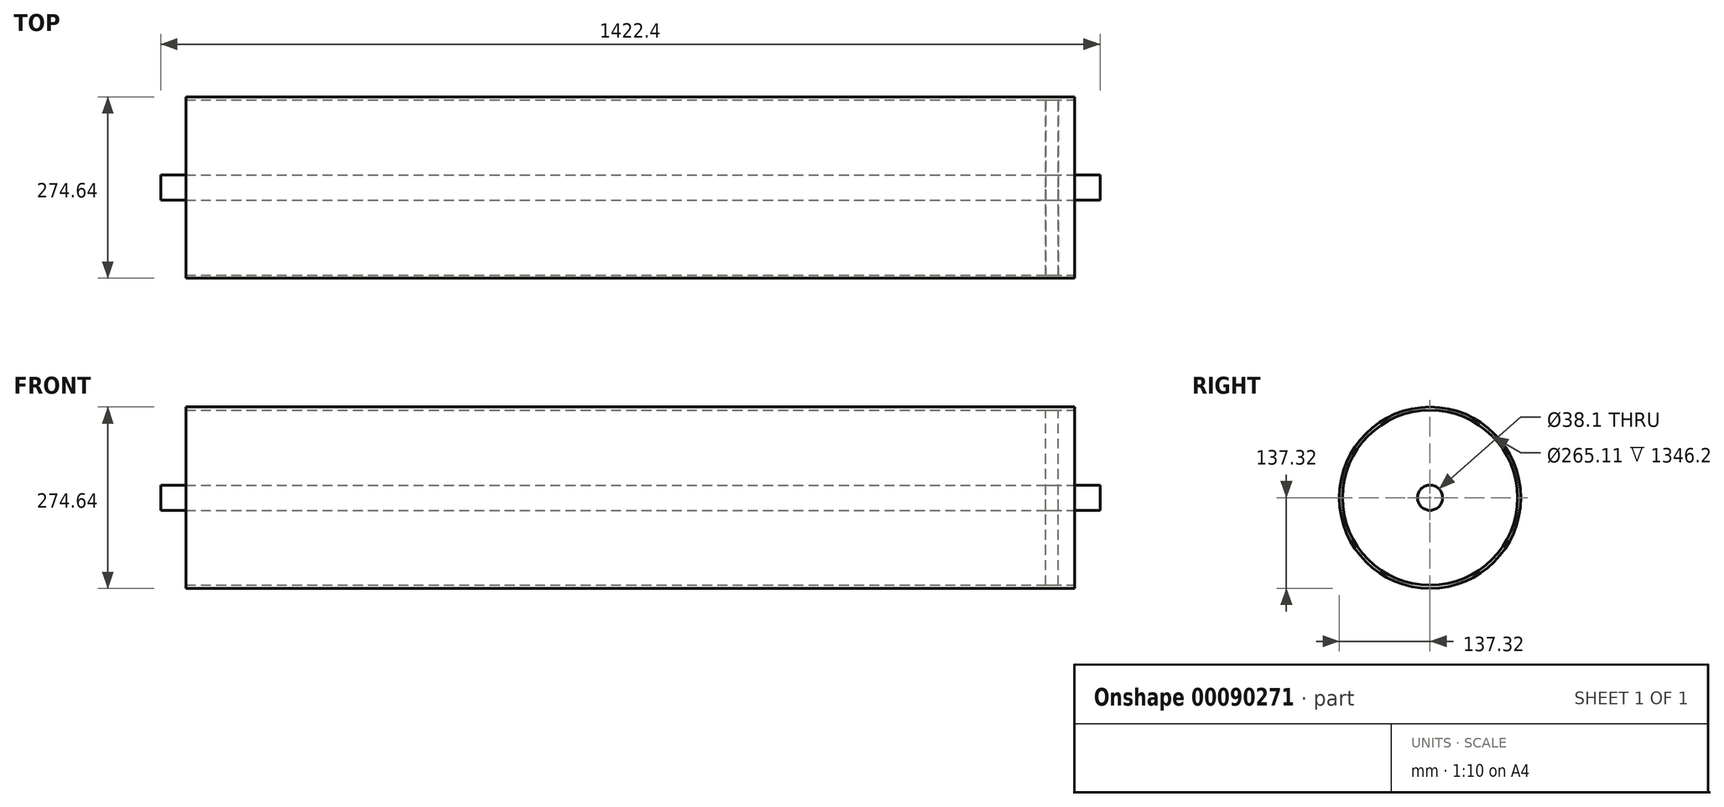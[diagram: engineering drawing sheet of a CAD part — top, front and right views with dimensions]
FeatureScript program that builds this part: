
annotation { "Feature Type Name" : "Feature", "Feature Type Description" : "" }
export const myFeature = defineFeature(function(context is Context, id is Id, definition is map)
    precondition{}
    {
        {
            var Q0;
            Q0=qCreatedBy(makeId("Top.planeOp"),FACE);
            var sketch = newSketch(context, id + "F0", { "sketchPlane" : qUnion([Q0])});
            skLineSegment(sketch, "E0.bottom", {"start": v(0, 0) * mm, "end": v(711.2, 0) * mm});
            skLineSegment(sketch, "E0.top", {"start": v(0, 19.05) * mm, "end": v(711.2, 19.05) * mm});
            skLineSegment(sketch, "E0.left", {"start": v(0, 0) * mm, "end": v(0, 19.05) * mm});
            skLineSegment(sketch, "E0.right", {"start": v(711.2, 0) * mm, "end": v(711.2, 19.05) * mm});
            skLineSegment(sketch, "E1.bottom", {"start": v(0, 137.32) * mm, "end": v(673.1, 137.32) * mm});
            skLineSegment(sketch, "E1.top", {"start": v(0, 132.56) * mm, "end": v(673.1, 132.56) * mm});
            skLineSegment(sketch, "E1.left", {"start": v(0, 137.32) * mm, "end": v(0, 132.56) * mm});
            skLineSegment(sketch, "E1.right", {"start": v(673.1, 137.32) * mm, "end": v(673.1, 132.56) * mm});
            skLineSegment(sketch, "E2", {"start": v(628.65, 19.05) * mm, "end": v(628.65, 132.56) * mm});
            skLineSegment(sketch, "E3", {"start": v(647.7, 132.56) * mm, "end": v(647.7, 19.05) * mm});
            skLineSegment(sketch, "E4.MirrorCS", {"start": v(-711.2, 0) * mm, "end": v(-711.2, 19.05) * mm});
            skLineSegment(sketch, "E5.MirrorCS", {"start": v(-673.1, 137.32) * mm, "end": v(-673.1, 132.56) * mm});
            skLineSegment(sketch, "E6.MirrorCS", {"start": v(0, 0) * mm, "end": v(-711.2, 0) * mm});
            skLineSegment(sketch, "E7.MirrorCS", {"start": v(-628.65, 19.05) * mm, "end": v(-628.65, 132.56) * mm});
            skLineSegment(sketch, "E8.MirrorCS", {"start": v(-647.7, 132.56) * mm, "end": v(-647.7, 19.05) * mm});
            skLineSegment(sketch, "E9.MirrorCS", {"start": v(0, 19.05) * mm, "end": v(-711.2, 19.05) * mm});
            skLineSegment(sketch, "E10.MirrorCS", {"start": v(0, 137.32) * mm, "end": v(-673.1, 137.32) * mm});
            skLineSegment(sketch, "E11.MirrorCS", {"start": v(0, 132.56) * mm, "end": v(-673.1, 132.56) * mm});
            skSolve(sketch);
        }
        {
            var Q0;
            {var subQ2=sQuery(id+"F0.wireOp",EDGE,"E0.left");Q0=makeQuery(id+"F0.imprint","IMPRINT",FACE,{"disambiguationData":[TD([[makeQuery(id+"F0.imprint","IMPRINT",EDGE,{"derivedFrom":subQ2}),1.0]])]});}
            var Q1;
            Q1=makeQuery(id+"F0.imprint","IMPRINT",FACE,{"disambiguationData":[TD([[makeQuery(id+"F0.imprint","IMPRINT",EDGE,{"derivedFrom":sQuery(id+"F0.wireOp",EDGE,"E0.bottom")}),1.0]])]});
            var Q2;
            Q2=sQuery(id+"F0.wireOp",EDGE,"E6.MirrorCS");
            revolve(context, id + "F1", {"entities" : qUnion([Q0, Q1]), "axis" : qUnion([Q2]), "revolveType" : RevolveType.FULL});
        }
        {
            var Q0;
            {var subQ0=sQuery(id+"F0.wireOp",EDGE,"E2");Q0=makeQuery(id+"F0.imprint","IMPRINT",FACE,{"disambiguationData":[TD([[makeQuery(id+"F0.imprint","IMPRINT",EDGE,{"derivedFrom":subQ0}),-1.0]])]});}
            var Q1;
            Q1=sQuery(id+"F0.wireOp",EDGE,"E6.MirrorCS");
            revolve(context, id + "F2", {"entities" : qUnion([Q0]), "axis" : qUnion([Q1]), "revolveType" : RevolveType.FULL});
        }
        {
            var Q0;
            {var subQ1=sQuery(id+"F0.wireOp",EDGE,"E1.left");Q0=makeQuery(id+"F0.imprint","IMPRINT",FACE,{"disambiguationData":[TD([[makeQuery(id+"F0.imprint","IMPRINT",EDGE,{"derivedFrom":subQ1}),-1.0]])]});}
            var Q1;
            Q1=makeQuery(id+"F0.imprint","IMPRINT",FACE,{"disambiguationData":[TD([[makeQuery(id+"F0.imprint","IMPRINT",EDGE,{"derivedFrom":sQuery(id+"F0.wireOp",EDGE,"E1.bottom")}),-1.0]])]});
            var Q2;
            Q2=sQuery(id+"F0.wireOp",EDGE,"E6.MirrorCS");
            revolve(context, id + "F3", {"entities" : qUnion([Q0, Q1]), "axis" : qUnion([Q2]), "revolveType" : RevolveType.FULL});
        }
    });
